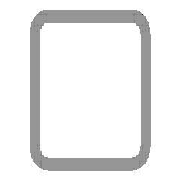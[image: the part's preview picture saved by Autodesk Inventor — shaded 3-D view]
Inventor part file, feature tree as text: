
AUTODESK INVENTOR PART (.ipt)
format: ipt  version: 2025.1 (Build 291241020, 241B)  size: 136,704 bytes
history: native  units: mm (DEFAULTED — no unit token found)
features: other x4, sketch x1, plane x1
ambient origin geometry x8: Origin, YZ Plane, XZ Plane, XY Plane, X Axis, Y Axis, Z Axis, Center Point
bodies: Solid1 (feature_tree), Body (feature_tree)
feature tree (6):
  parser-record x1  (decoder bookkeeping rows leaked as tree rows — omitted from the tree; the rows remain in map.json)
  other  "Driven Length"
  other  "Start plane"
  other  "End plane"
  sketch  "Sketch3"  dims[d3=850.0mm d4=0.0mm d7=6.0mm d9=100.0mm d11=100.0mm d12=3.0mm d13=50.0mm d14=900.0mm d15=50.0mm d16=50.0mm d17=90.0deg d18=850.0mm]
  plane  "Work Plane3"
